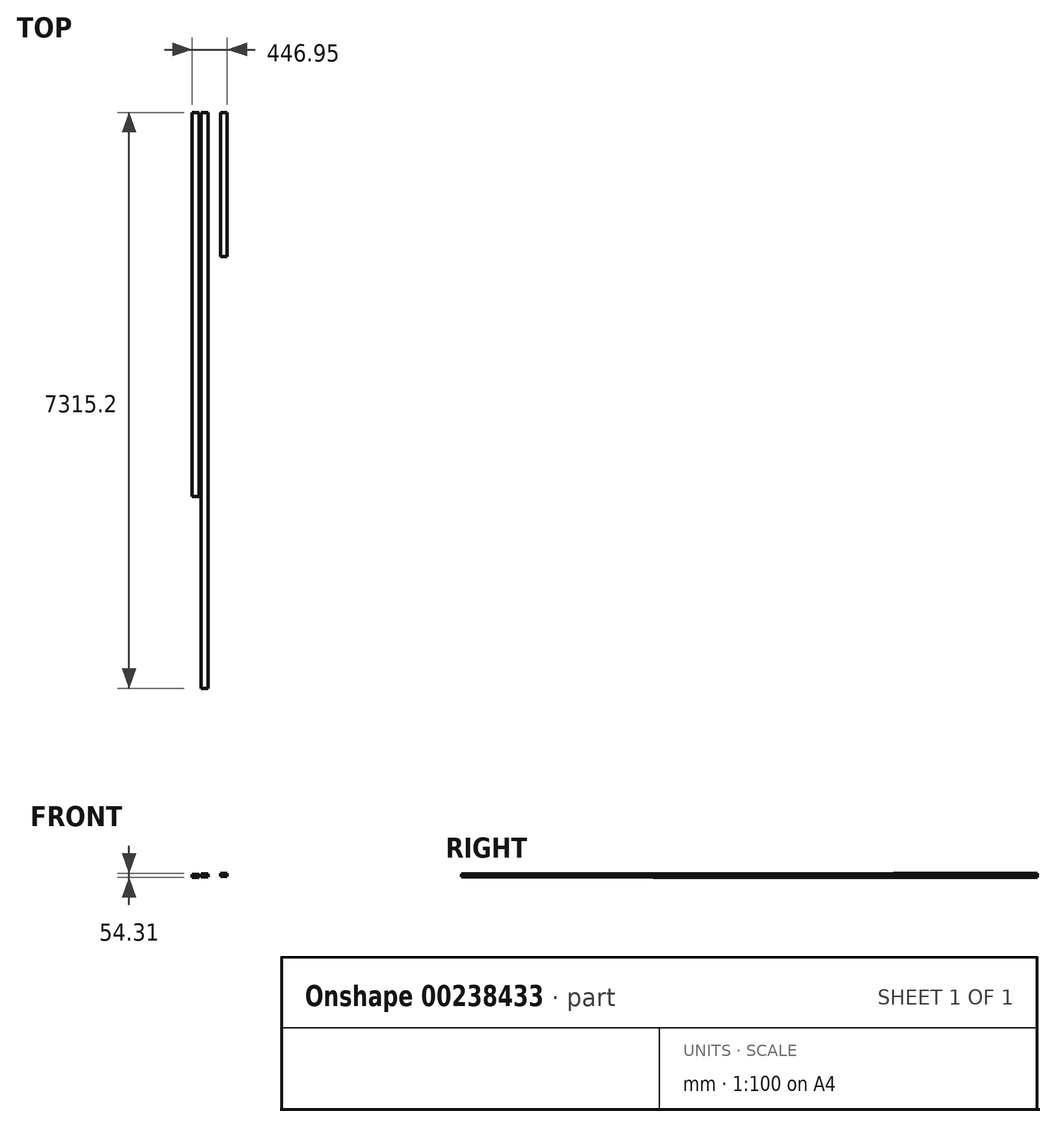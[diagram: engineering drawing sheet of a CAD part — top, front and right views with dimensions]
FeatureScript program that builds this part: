
annotation { "Feature Type Name" : "Feature", "Feature Type Description" : "" }
export const myFeature = defineFeature(function(context is Context, id is Id, definition is map)
    precondition{}
    {
        {
            var Q0;
            Q0=qCreatedBy(makeId("Front.planeOp"),FACE);
            var sketch = newSketch(context, id + "F0", { "sketchPlane" : qUnion([Q0])});
            skLineSegment(sketch, "E0.bottom", {"start": v(-79.77, 21.89) * mm, "end": v(9.13, 21.89) * mm});
            skLineSegment(sketch, "E0.top", {"start": v(-79.77, -16.21) * mm, "end": v(9.13, -16.21) * mm});
            skLineSegment(sketch, "E0.left", {"start": v(-79.77, 21.89) * mm, "end": v(-79.77, -16.21) * mm});
            skLineSegment(sketch, "E0.right", {"start": v(9.13, 21.89) * mm, "end": v(9.13, -16.21) * mm});
            skSolve(sketch);
        }
        {
            var Q0;
            Q0=makeQuery(id+"F0.imprint","IMPRINT",FACE,{"disambiguationData":[TD([[makeQuery(id+"F0.imprint","IMPRINT",EDGE,{"derivedFrom":sQuery(id+"F0.wireOp",EDGE,"E0.bottom")}),-1.0]])]});
            extrude(context, id + "F1", {"entities" : qUnion([Q0]), "depth" : 4876.8 * mm});
        }
        {
            var Q0;
            Q0=qCreatedBy(makeId("Front.planeOp"),FACE);
            var sketch = newSketch(context, id + "F2", { "sketchPlane" : qUnion([Q0])});
            skLineSegment(sketch, "E1.bottom", {"start": v(35.48, 30.9) * mm, "end": v(124.38, 30.9) * mm});
            skLineSegment(sketch, "E1.top", {"start": v(35.48, -7.2) * mm, "end": v(124.38, -7.2) * mm});
            skLineSegment(sketch, "E1.left", {"start": v(35.48, 30.9) * mm, "end": v(35.48, -7.2) * mm});
            skLineSegment(sketch, "E1.right", {"start": v(124.38, 30.9) * mm, "end": v(124.38, -7.2) * mm});
            skSolve(sketch);
        }
        {
            var Q0;
            Q0=makeQuery(id+"F2.imprint","IMPRINT",FACE,{"disambiguationData":[TD([[makeQuery(id+"F2.imprint","IMPRINT",EDGE,{"derivedFrom":sQuery(id+"F2.wireOp",EDGE,"E1.bottom")}),-1.0]])]});
            extrude(context, id + "F3", {"entities" : qUnion([Q0]), "depth" : 7315.2 * mm});
        }
        {
            var Q0;
            Q0=makeQuery(id+"F1.opExtrude","SWEPT_FACE",FACE,{"disambiguationData":[OSD([sQuery(id+"F0.wireOp",EDGE,"E0.bottom")])]});
            var sketch = newSketch(context, id + "F4", { "sketchPlane" : qUnion([Q0])});
            skCircle(sketch, "E2", {"center": v(-54.37, -25.4) * mm, "radius": 1.59 * mm});
            skCircle(sketch, "E3", {"center": v(-16.27, -25.4) * mm, "radius": 1.59 * mm});
            skCircle(sketch, "E4", {"center": v(-54.37, -4851.4) * mm, "radius": 1.59 * mm});
            skCircle(sketch, "E5", {"center": v(-16.27, -4851.4) * mm, "radius": 1.59 * mm});
            skSolve(sketch);
        }
        {
            var Q0;
            Q0=makeQuery(id+"F4.imprint","IMPRINT",FACE,{"disambiguationData":[TD([[makeQuery(id+"F4.imprint","IMPRINT",EDGE,{"derivedFrom":sQuery(id+"F4.wireOp",EDGE,"E5")}),1.0]])]});
            var Q1;
            Q1=makeQuery(id+"F4.imprint","IMPRINT",FACE,{"disambiguationData":[TD([[makeQuery(id+"F4.imprint","IMPRINT",EDGE,{"derivedFrom":sQuery(id+"F4.wireOp",EDGE,"E4")}),1.0]])]});
            var Q2;
            Q2=makeQuery(id+"F4.imprint","IMPRINT",FACE,{"disambiguationData":[TD([[makeQuery(id+"F4.imprint","IMPRINT",EDGE,{"derivedFrom":sQuery(id+"F4.wireOp",EDGE,"E2")}),1.0]])]});
            var Q3;
            Q3=makeQuery(id+"F4.imprint","IMPRINT",FACE,{"disambiguationData":[TD([[makeQuery(id+"F4.imprint","IMPRINT",EDGE,{"derivedFrom":sQuery(id+"F4.wireOp",EDGE,"E3")}),1.0]])]});
            extrude(context, id + "F5", {"entities" : qUnion([Q0, Q1, Q2, Q3]), "operationType" : NewBodyOperationType.REMOVE, "depth" : 25.4 * mm});
        }
        {
            var Q0;
            Q0=qCreatedBy(makeId("Front.planeOp"),FACE);
            var sketch = newSketch(context, id + "F6", { "sketchPlane" : qUnion([Q0])});
            skLineSegment(sketch, "E6.bottom", {"start": v(278.28, 38.1) * mm, "end": v(367.18, 38.1) * mm});
            skLineSegment(sketch, "E6.top", {"start": v(278.28, 0) * mm, "end": v(367.18, 0) * mm});
            skLineSegment(sketch, "E6.left", {"start": v(278.28, 38.1) * mm, "end": v(278.28, 0) * mm});
            skLineSegment(sketch, "E6.right", {"start": v(367.18, 38.1) * mm, "end": v(367.18, 0) * mm});
            skSolve(sketch);
        }
        {
            var Q0;
            Q0=makeQuery(id+"F6.imprint","IMPRINT",FACE,{"disambiguationData":[TD([[makeQuery(id+"F6.imprint","IMPRINT",EDGE,{"derivedFrom":sQuery(id+"F6.wireOp",EDGE,"E6.bottom")}),-1.0]])]});
            extrude(context, id + "F7", {"entities" : qUnion([Q0]), "depth" : 1828.8 * mm});
        }
    });
